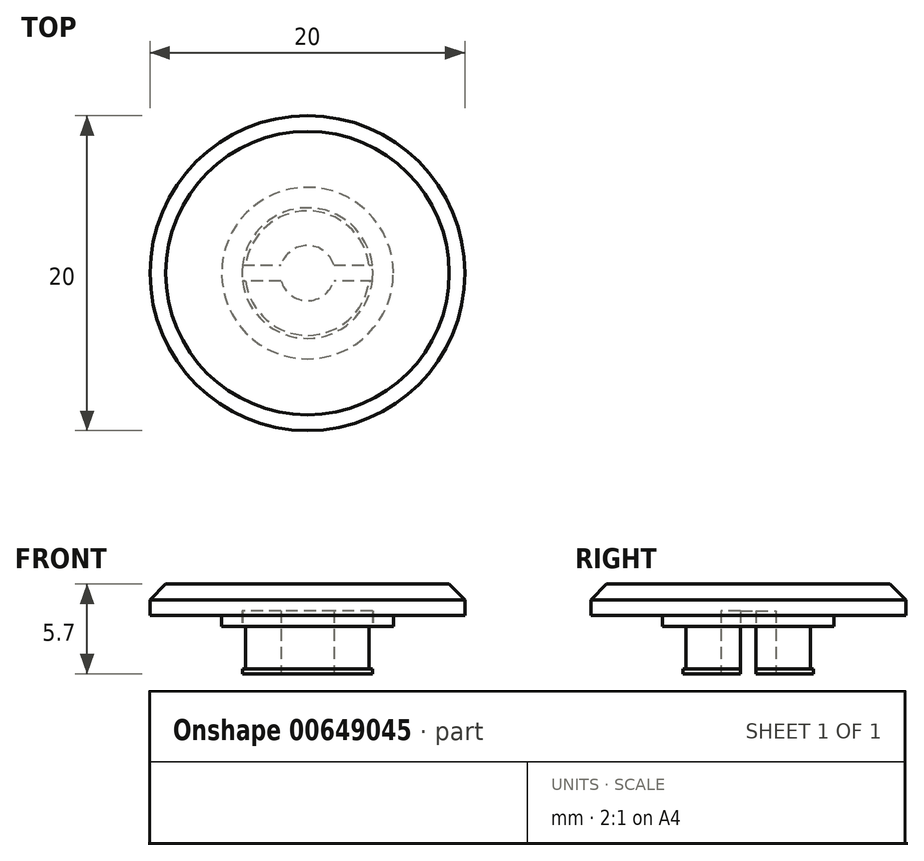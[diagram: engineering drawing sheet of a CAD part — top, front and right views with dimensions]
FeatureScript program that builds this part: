
annotation { "Feature Type Name" : "Feature", "Feature Type Description" : "" }
export const myFeature = defineFeature(function(context is Context, id is Id, definition is map)
    precondition{}
    {
        {
            var Q0;
            Q0=qCreatedBy(makeId("Front.planeOp"),FACE);
            var sketch = newSketch(context, id + "F0", { "sketchPlane" : qUnion([Q0])});
            skLineSegment(sketch, "E0", {"start": v(-17.03, 15.94) * mm, "end": v(-27.03, 15.94) * mm});
            skLineSegment(sketch, "E1", {"start": v(-27.03, 15.94) * mm, "end": v(-27.03, 13.94) * mm});
            skLineSegment(sketch, "E2", {"start": v(-27.03, 13.94) * mm, "end": v(-22.48, 13.94) * mm});
            skLineSegment(sketch, "E3", {"start": v(-22.48, 13.94) * mm, "end": v(-22.48, 13.24) * mm});
            skLineSegment(sketch, "E4", {"start": v(-22.48, 13.24) * mm, "end": v(-20.98, 13.24) * mm});
            skLineSegment(sketch, "E5", {"start": v(-20.98, 13.24) * mm, "end": v(-20.98, 10.54) * mm});
            skLineSegment(sketch, "E6", {"start": v(-20.98, 10.54) * mm, "end": v(-21.18, 10.54) * mm});
            skLineSegment(sketch, "E7", {"start": v(-21.18, 10.54) * mm, "end": v(-21.18, 10.24) * mm});
            skLineSegment(sketch, "E8", {"start": v(-21.18, 10.24) * mm, "end": v(-17.03, 10.24) * mm});
            skLineSegment(sketch, "E9", {"start": v(-17.03, 15.94) * mm, "end": v(-17.03, 10.24) * mm});
            skSolve(sketch);
        }
        {
            var Q0;
            Q0=makeQuery(id+"F0.imprint","IMPRINT",FACE,{"disambiguationData":[TD([[makeQuery(id+"F0.imprint","IMPRINT",EDGE,{"derivedFrom":sQuery(id+"F0.wireOp",EDGE,"E0")}),1.0]])]});
            var Q1;
            Q1=sQuery(id+"F0.wireOp",EDGE,"E9");
            revolve(context, id + "F1", {"entities" : qUnion([Q0]), "axis" : qUnion([Q1]), "revolveType" : RevolveType.FULL});
        }
        {
            var Q0;
            Q0=makeQuery(id+"F1.opRevolve","SWEPT_FACE",FACE,{"disambiguationData":[OSD([sQuery(id+"F0.wireOp",EDGE,"E8")])]});
            var sketch = newSketch(context, id + "F2", { "sketchPlane" : qUnion([Q0])});
            skArc(sketch, "E10", {"start": v(-18.7, -0.5) * mm, "mid": v(-17.03, -1.75) * mm, "end": v(-15.35, -0.5) * mm});
            skLineSegment(sketch, "E11", {"start": v(-21.99, -0.5) * mm, "end": v(-18.7, -0.5) * mm});
            skLineSegment(sketch, "E12", {"start": v(-12.03, -0.5) * mm, "end": v(-12.03, 0.5) * mm});
            skLineSegment(sketch, "E13", {"start": v(-12.03, 0.5) * mm, "end": v(-15.35, 0.5) * mm});
            skLineSegment(sketch, "E14", {"start": v(-21.99, 0.5) * mm, "end": v(-21.99, -0.5) * mm});
            skArc(sketch, "E15.trimOffspring", {"start": v(-15.35, 0.5) * mm, "mid": v(-17.03, 1.75) * mm, "end": v(-18.7, 0.5) * mm});
            skLineSegment(sketch, "E16.trimOffspring", {"start": v(-18.7, 0.5) * mm, "end": v(-21.99, 0.5) * mm});
            skLineSegment(sketch, "E17.trimOffspring", {"start": v(-15.35, -0.5) * mm, "end": v(-12.03, -0.5) * mm});
            skSolve(sketch);
        }
        {
            var Q0;
            {var subQ2=sQuery(id+"F2.wireOp",EDGE,"E10");Q0=makeQuery(id+"F2.imprint","IMPRINT",FACE,{"disambiguationData":[TD([[makeQuery(id+"F2.imprint","IMPRINT",EDGE,{"derivedFrom":subQ2}),1.0]])]});}
            extrude(context, id + "F3", {"entities" : qUnion([Q0]), "operationType" : NewBodyOperationType.REMOVE, "oppositeDirection" : true, "depth" : 4 * mm, "offsetDistance" : 25 * mm});
        }
        {
            var Q0;
            Q0=makeQuery(id+"F1.opRevolve","SWEPT_FACE",FACE,{"disambiguationData":[OSD([sQuery(id+"F0.wireOp",EDGE,"E0")])]});
            chamfer(context, id + "F4", {"entities" : qUnion([Q0]), "width" : 1 * mm, "tangentPropagation" : true});
        }
    });
